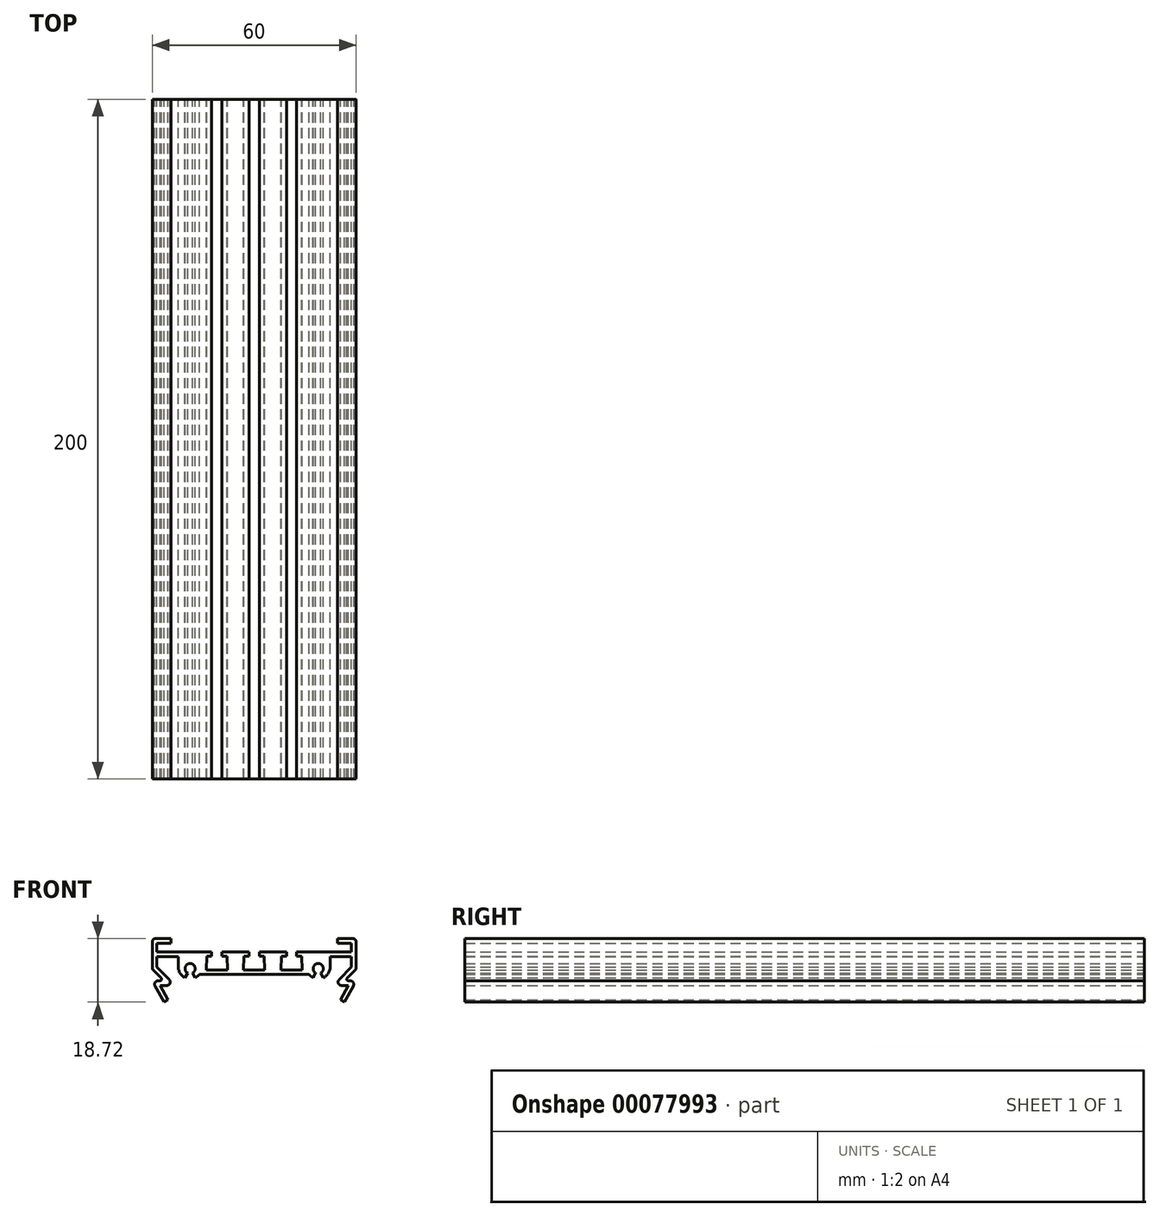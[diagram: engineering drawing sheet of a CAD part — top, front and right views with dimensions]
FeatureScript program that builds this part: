
annotation { "Feature Type Name" : "Feature", "Feature Type Description" : "" }
export const myFeature = defineFeature(function(context is Context, id is Id, definition is map)
    precondition{}
    {
        {
            var Q0;
            Q0=qCreatedBy(makeId("Front.planeOp"),FACE);
            var sketch = newSketch(context, id + "F0", { "sketchPlane" : qUnion([Q0])});
            skLineSegment(sketch, "E0", {"start": v(-17.32, -2.14) * mm, "end": v(-18.1, -0.8) * mm});
            skArc(sketch, "E1", {"start": v(-18.1, -0.8) * mm, "mid": v(-18.85, 2) * mm, "end": v(-19.6, -0.8) * mm});
            skLineSegment(sketch, "E2", {"start": v(-19.6, -0.8) * mm, "end": v(-20.38, -2.14) * mm});
            skArc(sketch, "E3", {"start": v(-22.35, 1) * mm, "mid": v(-21.82, -0.85) * mm, "end": v(-20.38, -2.14) * mm});
            skLineSegment(sketch, "E4", {"start": v(-22.35, 1) * mm, "end": v(-22.35, 4) * mm});
            skArc(sketch, "E5", {"start": v(-25.7, -4.45) * mm, "mid": v(-24.78, -3.83) * mm, "end": v(-25, -2.74) * mm});
            skArc(sketch, "E6", {"start": v(-28.3, -3.1) * mm, "mid": v(-29.17, -3.59) * mm, "end": v(-29.18, -4.58) * mm});
            skArc(sketch, "E7", {"start": v(-27.75, -3.1) * mm, "mid": v(-27.3, -2.79) * mm, "end": v(-27.4, -2.24) * mm});
            skArc(sketch, "E8", {"start": v(-30, 0.77) * mm, "mid": v(-29.92, 0.39) * mm, "end": v(-29.7, 0.06) * mm});
            skArc(sketch, "E9", {"start": v(-29, 9.36) * mm, "mid": v(-29.7, 9.06) * mm, "end": v(-30, 8.36) * mm});
            skLineSegment(sketch, "E10", {"start": v(-24.5, 9.36) * mm, "end": v(-29, 9.36) * mm});
            skLineSegment(sketch, "E11", {"start": v(-24.5, 9.36) * mm, "end": v(-24.5, 8) * mm});
            skLineSegment(sketch, "E12", {"start": v(-24.5, 8) * mm, "end": v(-28.65, 8) * mm});
            skLineSegment(sketch, "E13", {"start": v(-28.65, 8) * mm, "end": v(-28.65, 5.36) * mm});
            skLineSegment(sketch, "E14", {"start": v(3.12, 0.1) * mm, "end": v(3, 4.1) * mm});
            skLineSegment(sketch, "E15", {"start": v(3, 4.1) * mm, "end": v(1.5, 4.1) * mm});
            skLineSegment(sketch, "E16", {"start": v(1.5, 4.1) * mm, "end": v(1.5, 5.36) * mm});
            skLineSegment(sketch, "E17", {"start": v(1.5, 5.36) * mm, "end": v(9.5, 5.36) * mm});
            skLineSegment(sketch, "E18", {"start": v(9.5, 5.36) * mm, "end": v(9.5, 4.1) * mm});
            skLineSegment(sketch, "E19", {"start": v(9.5, 4.1) * mm, "end": v(8, 4.1) * mm});
            skLineSegment(sketch, "E20", {"start": v(8, 4.1) * mm, "end": v(7.88, 0.1) * mm});
            skLineSegment(sketch, "E21", {"start": v(7.88, 0.1) * mm, "end": v(14.12, 0.1) * mm});
            skLineSegment(sketch, "E22", {"start": v(14.12, 0.1) * mm, "end": v(14, 4.1) * mm});
            skLineSegment(sketch, "E23", {"start": v(14, 4.1) * mm, "end": v(12.5, 4.1) * mm});
            skLineSegment(sketch, "E24", {"start": v(12.5, 4.1) * mm, "end": v(12.5, 5.36) * mm});
            skLineSegment(sketch, "E25", {"start": v(28.65, 8) * mm, "end": v(28.65, 5.36) * mm});
            skLineSegment(sketch, "E26", {"start": v(24.5, 8) * mm, "end": v(28.65, 8) * mm});
            skLineSegment(sketch, "E27", {"start": v(24.5, 9.36) * mm, "end": v(24.5, 8) * mm});
            skLineSegment(sketch, "E28", {"start": v(24.5, 9.36) * mm, "end": v(29, 9.36) * mm});
            skArc(sketch, "E29", {"start": v(30, 8.36) * mm, "mid": v(29.7, 9.06) * mm, "end": v(29, 9.36) * mm});
            skLineSegment(sketch, "E30", {"start": v(30, 8.36) * mm, "end": v(30, 0.77) * mm});
            skArc(sketch, "E31", {"start": v(29.7, 0.06) * mm, "mid": v(29.92, 0.39) * mm, "end": v(30, 0.77) * mm});
            skLineSegment(sketch, "E32", {"start": v(29.7, 0.06) * mm, "end": v(27.4, -2.24) * mm});
            skArc(sketch, "E33", {"start": v(27.4, -2.24) * mm, "mid": v(27.3, -2.79) * mm, "end": v(27.75, -3.1) * mm});
            skLineSegment(sketch, "E34", {"start": v(27.75, -3.1) * mm, "end": v(28.3, -3.1) * mm});
            skArc(sketch, "E35", {"start": v(29.18, -4.58) * mm, "mid": v(29.17, -3.59) * mm, "end": v(28.3, -3.1) * mm});
            skLineSegment(sketch, "E36", {"start": v(29.18, -4.58) * mm, "end": v(26.55, -9.36) * mm});
            skLineSegment(sketch, "E37", {"start": v(25.37, -8.7) * mm, "end": v(26.55, -9.36) * mm});
            skLineSegment(sketch, "E38", {"start": v(27.71, -4.45) * mm, "end": v(25.37, -8.7) * mm});
            skLineSegment(sketch, "E39", {"start": v(25.7, -4.45) * mm, "end": v(27.71, -4.45) * mm});
            skArc(sketch, "E40", {"start": v(25, -2.74) * mm, "mid": v(24.78, -3.83) * mm, "end": v(25.7, -4.45) * mm});
            skLineSegment(sketch, "E41", {"start": v(28.65, 0.92) * mm, "end": v(25, -2.74) * mm});
            skLineSegment(sketch, "E42", {"start": v(28.65, 4) * mm, "end": v(28.65, 0.92) * mm});
            skLineSegment(sketch, "E43", {"start": v(22.35, 4) * mm, "end": v(28.65, 4) * mm});
            skLineSegment(sketch, "E44", {"start": v(22.35, 4) * mm, "end": v(22.35, 1) * mm});
            skLineSegment(sketch, "E45", {"start": v(20.38, -2.14) * mm, "end": v(19.6, -0.8) * mm});
            skArc(sketch, "E46", {"start": v(19.6, -0.8) * mm, "mid": v(18.85, 2) * mm, "end": v(18.1, -0.8) * mm});
            skLineSegment(sketch, "E47", {"start": v(18.1, -0.8) * mm, "end": v(17.32, -2.14) * mm});
            skArc(sketch, "E48", {"start": v(16.17, -1.24) * mm, "mid": v(16.7, -1.75) * mm, "end": v(17.32, -2.14) * mm});
            skLineSegment(sketch, "E49", {"start": v(-27.75, -3.1) * mm, "end": v(-28.3, -3.1) * mm});
            skLineSegment(sketch, "E50", {"start": v(-29.7, 0.06) * mm, "end": v(-27.4, -2.24) * mm});
            skLineSegment(sketch, "E51", {"start": v(-30, 8.36) * mm, "end": v(-30, 0.77) * mm});
            skLineSegment(sketch, "E52", {"start": v(-12.5, 5.36) * mm, "end": v(-28.65, 5.36) * mm});
            skLineSegment(sketch, "E53", {"start": v(-12.5, 4.1) * mm, "end": v(-12.5, 5.36) * mm});
            skLineSegment(sketch, "E54", {"start": v(-14, 4.1) * mm, "end": v(-12.5, 4.1) * mm});
            skLineSegment(sketch, "E55", {"start": v(-14.12, 0.1) * mm, "end": v(-14, 4.1) * mm});
            skLineSegment(sketch, "E56", {"start": v(-7.88, 0.1) * mm, "end": v(-14.12, 0.1) * mm});
            skLineSegment(sketch, "E57", {"start": v(-8, 4.1) * mm, "end": v(-7.88, 0.1) * mm});
            skLineSegment(sketch, "E58", {"start": v(-9.5, 4.1) * mm, "end": v(-8, 4.1) * mm});
            skLineSegment(sketch, "E59", {"start": v(-9.5, 5.36) * mm, "end": v(-9.5, 4.1) * mm});
            skLineSegment(sketch, "E60", {"start": v(-1.5, 5.36) * mm, "end": v(-9.5, 5.36) * mm});
            skLineSegment(sketch, "E61", {"start": v(-1.5, 4.1) * mm, "end": v(-1.5, 5.36) * mm});
            skLineSegment(sketch, "E62", {"start": v(-3, 4.1) * mm, "end": v(-1.5, 4.1) * mm});
            skLineSegment(sketch, "E63", {"start": v(-3.12, 0.1) * mm, "end": v(-3, 4.1) * mm});
            skLineSegment(sketch, "E64", {"start": v(3.12, 0.1) * mm, "end": v(-3.12, 0.1) * mm});
            skLineSegment(sketch, "E65", {"start": v(16.17, -1.24) * mm, "end": v(-16.17, -1.24) * mm});
            skLineSegment(sketch, "E66", {"start": v(-22.35, 4) * mm, "end": v(-28.65, 4) * mm});
            skLineSegment(sketch, "E67", {"start": v(-28.65, 4) * mm, "end": v(-28.65, 0.92) * mm});
            skLineSegment(sketch, "E68", {"start": v(-28.65, 0.92) * mm, "end": v(-25, -2.74) * mm});
            skLineSegment(sketch, "E69", {"start": v(-25.7, -4.45) * mm, "end": v(-27.71, -4.45) * mm});
            skLineSegment(sketch, "E70", {"start": v(-27.71, -4.45) * mm, "end": v(-25.37, -8.7) * mm});
            skLineSegment(sketch, "E71", {"start": v(-25.37, -8.7) * mm, "end": v(-26.55, -9.36) * mm});
            skLineSegment(sketch, "E72", {"start": v(-29.18, -4.58) * mm, "end": v(-26.55, -9.36) * mm});
            skLineSegment(sketch, "E73", {"start": v(12.5, 5.36) * mm, "end": v(28.65, 5.36) * mm});
            skArc(sketch, "E74", {"start": v(-17.32, -2.14) * mm, "mid": v(-16.7, -1.75) * mm, "end": v(-16.17, -1.24) * mm});
            skArc(sketch, "E75", {"start": v(20.38, -2.14) * mm, "mid": v(21.82, -0.85) * mm, "end": v(22.35, 1) * mm});
            skSolve(sketch);
        }
        {
            var Q0;
            Q0=qSketchRegion(id+"F0",true);
            extrude(context, id + "F1", {"entities" : qUnion([Q0]), "depth" : 200 * mm});
        }
    });
